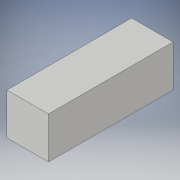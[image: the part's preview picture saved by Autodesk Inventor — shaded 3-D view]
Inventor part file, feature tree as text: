
AUTODESK INVENTOR PART (.ipt)
format: ipt  version: 2018.2 (Build 222227000, 227)  size: 88,576 bytes
history: native  units: mm
features: other x1, extrude x1, sketch x1
ambient origin geometry x8: Origin, YZ Plane, XZ Plane, XY Plane, X Axis, Y Axis, Z Axis, Center Point
bodies: Body1 (feature_tree)
feature tree (3):
  other  "ソリッド1"
  extrude  "押し出し1"  Depth=6000.0mm
  sketch  "スケッチ1"
